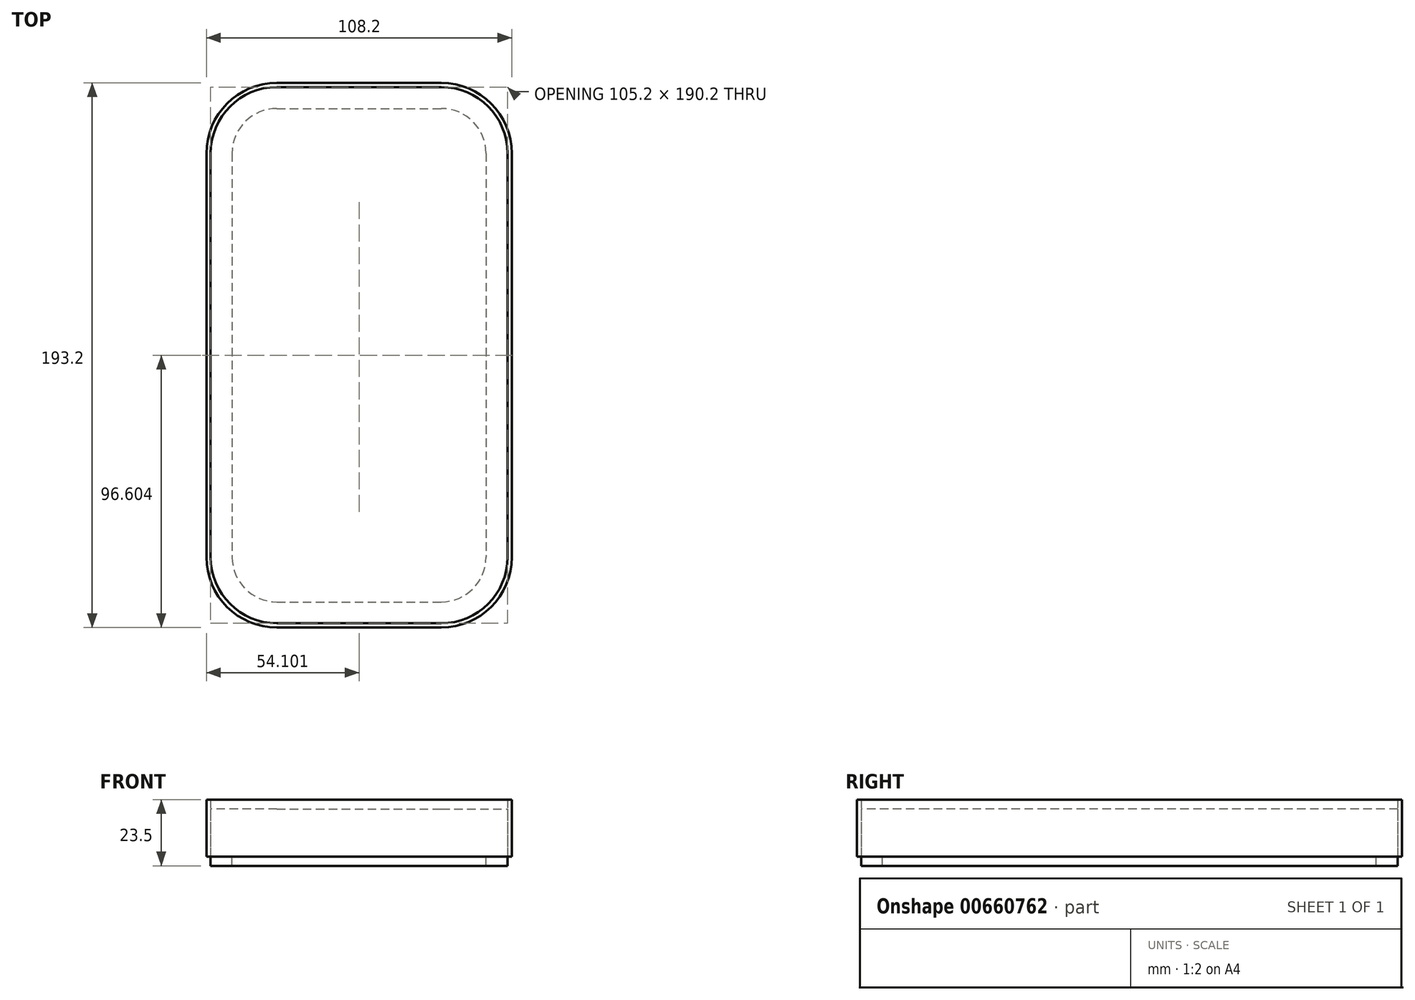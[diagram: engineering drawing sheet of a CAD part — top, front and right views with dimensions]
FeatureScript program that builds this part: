
annotation { "Feature Type Name" : "Feature", "Feature Type Description" : "" }
export const myFeature = defineFeature(function(context is Context, id is Id, definition is map)
    precondition{}
    {
        {
            var Q0;
            Q0=qCreatedBy(makeId("Top.planeOp"),FACE);
            var sketch = newSketch(context, id + "F0", { "sketchPlane" : qUnion([Q0])});
            skLineSegment(sketch, "E0.bottom", {"start": v(-39.58, 89.8) * mm, "end": v(18.67, 89.8) * mm});
            skLineSegment(sketch, "E0.top", {"start": v(-39.58, -85.2) * mm, "end": v(18.67, -85.2) * mm});
            skLineSegment(sketch, "E0.left", {"start": v(-55.46, 73.93) * mm, "end": v(-55.46, -69.32) * mm});
            skLineSegment(sketch, "E0.right", {"start": v(34.54, 73.93) * mm, "end": v(34.54, -69.32) * mm});
            skPoint(sketch, "E1.visualSharp", {"position": v(-55.46, 89.8) * mm});
            skArc(sketch, "E1.filletArc", {"start": v(-39.58, 89.8) * mm, "mid": v(-50.8, 85.15) * mm, "end": v(-55.46, 73.93) * mm});
            skPoint(sketch, "E2.visualSharp", {"position": v(34.54, 89.8) * mm});
            skArc(sketch, "E2.filletArc", {"start": v(34.54, 73.93) * mm, "mid": v(29.9, 85.15) * mm, "end": v(18.67, 89.8) * mm});
            skPoint(sketch, "E3.visualSharp", {"position": v(-55.46, -85.2) * mm});
            skArc(sketch, "E3.filletArc", {"start": v(-55.46, -69.32) * mm, "mid": v(-50.8, -80.55) * mm, "end": v(-39.58, -85.2) * mm});
            skPoint(sketch, "E4.visualSharp", {"position": v(34.54, -85.2) * mm});
            skArc(sketch, "E4.filletArc", {"start": v(18.67, -85.2) * mm, "mid": v(29.9, -80.55) * mm, "end": v(34.54, -69.32) * mm});
            skArc(sketch, "E5.0", {"start": v(-39.58, 97.4) * mm, "mid": v(-56.18, 90.53) * mm, "end": v(-63.06, 73.93) * mm});
            skLineSegment(sketch, "E5.1", {"start": v(-63.06, 73.93) * mm, "end": v(-63.06, -69.32) * mm});
            skLineSegment(sketch, "E5.2", {"start": v(-39.58, 97.4) * mm, "end": v(18.67, 97.4) * mm});
            skArc(sketch, "E5.3", {"start": v(-63.06, -69.32) * mm, "mid": v(-56.18, -85.92) * mm, "end": v(-39.58, -92.8) * mm});
            skArc(sketch, "E5.4", {"start": v(42.14, 73.93) * mm, "mid": v(35.27, 90.53) * mm, "end": v(18.67, 97.4) * mm});
            skLineSegment(sketch, "E5.5", {"start": v(42.14, 73.93) * mm, "end": v(42.14, -69.32) * mm});
            skArc(sketch, "E5.6", {"start": v(18.67, -92.8) * mm, "mid": v(35.27, -85.92) * mm, "end": v(42.14, -69.32) * mm});
            skLineSegment(sketch, "E5.7", {"start": v(-39.58, -92.8) * mm, "end": v(18.67, -92.8) * mm});
            skArc(sketch, "E6.0", {"start": v(-39.58, 98.9) * mm, "mid": v(-57.24, 91.59) * mm, "end": v(-64.56, 73.93) * mm});
            skLineSegment(sketch, "E6.1", {"start": v(-39.58, 98.9) * mm, "end": v(18.67, 98.9) * mm});
            skLineSegment(sketch, "E6.2", {"start": v(-64.56, 73.93) * mm, "end": v(-64.56, -69.32) * mm});
            skArc(sketch, "E6.3", {"start": v(43.64, 73.93) * mm, "mid": v(36.33, 91.59) * mm, "end": v(18.67, 98.9) * mm});
            skArc(sketch, "E6.4", {"start": v(-64.56, -69.32) * mm, "mid": v(-57.24, -86.98) * mm, "end": v(-39.58, -94.3) * mm});
            skLineSegment(sketch, "E6.5", {"start": v(-39.58, -94.3) * mm, "end": v(18.67, -94.3) * mm});
            skArc(sketch, "E6.6", {"start": v(18.67, -94.3) * mm, "mid": v(36.33, -86.98) * mm, "end": v(43.64, -69.32) * mm});
            skLineSegment(sketch, "E6.7", {"start": v(43.64, 73.93) * mm, "end": v(43.64, -69.32) * mm});
            skSolve(sketch);
        }
        {
            var Q0;
            Q0=makeQuery(id+"F0.imprint","IMPRINT",FACE,{"disambiguationData":[TD([[makeQuery(id+"F0.imprint","IMPRINT",EDGE,{"derivedFrom":sQuery(id+"F0.wireOp",EDGE,"E0.bottom")}),-1.0]])]});
            var Q1;
            Q1=makeQuery(id+"F0.imprint","IMPRINT",FACE,{"disambiguationData":[TD([[makeQuery(id+"F0.imprint","IMPRINT",EDGE,{"derivedFrom":sQuery(id+"F0.wireOp",EDGE,"E0.bottom")}),1.0]])]});
            extrude(context, id + "F1", {"entities" : qUnion([Q0, Q1]), "depth" : 17 * mm, "offsetDistance" : 25 * mm});
        }
        {
            var Q0;
            Q0=makeQuery(id+"F0.imprint","IMPRINT",FACE,{"disambiguationData":[TD([[makeQuery(id+"F0.imprint","IMPRINT",EDGE,{"derivedFrom":sQuery(id+"F0.wireOp",EDGE,"E0.bottom")}),1.0]])]});
            extrude(context, id + "F2", {"entities" : qUnion([Q0]), "operationType" : NewBodyOperationType.ADD, "oppositeDirection" : true, "depth" : 3.2 * mm, "offsetDistance" : 25 * mm});
        }
        {
            var Q0;
            Q0=makeQuery(id+"F0.imprint","IMPRINT",FACE,{"disambiguationData":[TD([[makeQuery(id+"F0.imprint","IMPRINT",EDGE,{"derivedFrom":sQuery(id+"F0.wireOp",EDGE,"E5.0")}),-1.0]])]});
            extrude(context, id + "F3", {"entities" : qUnion([Q0]), "depth" : 20.3 * mm, "offsetDistance" : 25 * mm});
        }
    });
